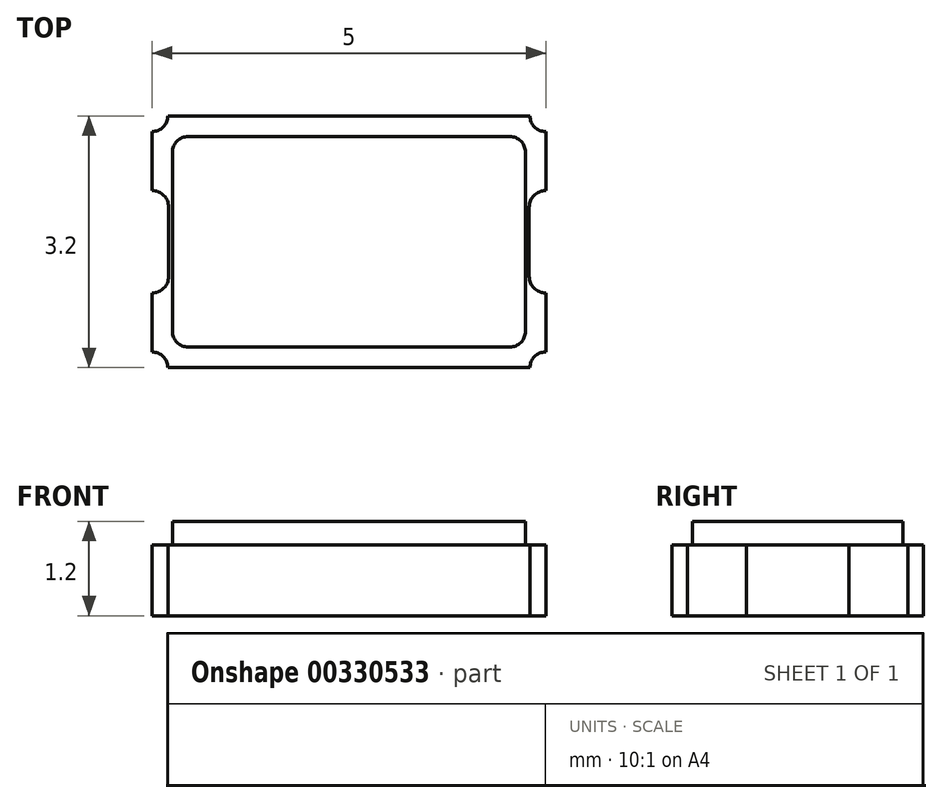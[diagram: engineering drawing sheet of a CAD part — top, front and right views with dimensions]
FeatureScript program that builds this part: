
annotation { "Feature Type Name" : "Feature", "Feature Type Description" : "" }
export const myFeature = defineFeature(function(context is Context, id is Id, definition is map)
    precondition{}
    {
        {
            var Q0;
            Q0=qCreatedBy(makeId("Top.planeOp"),FACE);
            var sketch = newSketch(context, id + "F0", { "sketchPlane" : qUnion([Q0])});
            skLineSegment(sketch, "E0.bottom", {"start": v(0, -1.6) * mm, "end": v(-2.3, -1.6) * mm});
            skLineSegment(sketch, "E0.top", {"start": v(0, 1.6) * mm, "end": v(-2.3, 1.6) * mm});
            skPoint(sketch, "E0.middle", {"position": v(0, 0) * mm});
            skArc(sketch, "E1", {"start": v(-2.3, 1.6) * mm, "mid": v(-2.36, 1.46) * mm, "end": v(-2.5, 1.4) * mm});
            skArc(sketch, "E2", {"start": v(-2.5, -1.4) * mm, "mid": v(-2.36, -1.46) * mm, "end": v(-2.3, -1.6) * mm});
            skLineSegment(sketch, "E3", {"start": v(0, 0) * mm, "end": v(-3.2, 0) * mm, "construction": true});
            skLineSegment(sketch, "E4", {"start": v(-2.5, 1.4) * mm, "end": v(-2.5, 0.65) * mm});
            skPoint(sketch, "E5.endSnap0", {"position": v(0, 1.6) * mm});
            skLineSegment(sketch, "E6", {"start": v(0, 1.6) * mm, "end": v(0, -2.23) * mm, "construction": true});
            skLineSegment(sketch, "E7.left", {"start": v(-2.3, -0.44) * mm, "end": v(-2.3, 0.44) * mm});
            skPoint(sketch, "E7.middle", {"position": v(-2.5, 0) * mm});
            skArc(sketch, "E8", {"start": v(-2.3, 0.44) * mm, "mid": v(-2.35, 0.59) * mm, "end": v(-2.5, 0.65) * mm});
            skArc(sketch, "E9", {"start": v(-2.3, -0.44) * mm, "mid": v(-2.35, -0.59) * mm, "end": v(-2.5, -0.65) * mm});
            skLineSegment(sketch, "E10.trimOffspring", {"start": v(-2.5, -0.65) * mm, "end": v(-2.5, -1.4) * mm});
            skPoint(sketch, "E11.orphan", {"position": v(-2.7, -0.44) * mm});
            skLineSegment(sketch, "E12.MirrorCS", {"start": v(2.5, -0.65) * mm, "end": v(2.5, -1.4) * mm});
            skLineSegment(sketch, "E13.MirrorCS", {"start": v(0, 0) * mm, "end": v(3.2, 0) * mm, "construction": true});
            skPoint(sketch, "E14.MirrorP", {"position": v(2.5, 0) * mm});
            skLineSegment(sketch, "E15.MirrorCS", {"start": v(2.5, 1.4) * mm, "end": v(2.5, 0.65) * mm});
            skLineSegment(sketch, "E16.MirrorCS", {"start": v(0, 1.6) * mm, "end": v(2.3, 1.6) * mm});
            skArc(sketch, "E17.MirrorCS", {"start": v(2.5, -1.4) * mm, "mid": v(2.36, -1.46) * mm, "end": v(2.3, -1.6) * mm});
            skLineSegment(sketch, "E18.MirrorCS", {"start": v(0, -1.6) * mm, "end": v(2.3, -1.6) * mm});
            skArc(sketch, "E19.MirrorCS", {"start": v(2.3, -0.44) * mm, "mid": v(2.35, -0.59) * mm, "end": v(2.5, -0.65) * mm});
            skLineSegment(sketch, "E20.MirrorCS", {"start": v(2.3, -0.44) * mm, "end": v(2.3, 0.44) * mm});
            skArc(sketch, "E21.MirrorCS", {"start": v(2.3, 0.44) * mm, "mid": v(2.35, 0.59) * mm, "end": v(2.5, 0.65) * mm});
            skPoint(sketch, "E22.MirrorP", {"position": v(2.7, -0.44) * mm});
            skArc(sketch, "E23.MirrorCS", {"start": v(2.3, 1.6) * mm, "mid": v(2.36, 1.46) * mm, "end": v(2.5, 1.4) * mm});
            skSolve(sketch);
        }
        {
            var Q0;
            Q0 = qSketchRegion(id + "F0", true);
            extrude(context, id + "F1", {"entities" : qUnion([Q0]), "depth" : .9 * mm, "offsetDistance" : 25 * mm});
        }
        {
            var Q0;
            Q0=makeQuery(id+"F1.opExtrude","CAP_FACE",FACE,{"disambiguationData":[OSD([sQuery(id+"F0.wireOp",EDGE,"E0.bottom"),sQuery(id+"F0.wireOp",EDGE,"E0.top"),sQuery(id+"F0.wireOp",EDGE,"E0.left"),sQuery(id+"F0.wireOp",EDGE,"E0.right"),sQuery(id+"F0.wireOp",EDGE,"E1"),sQuery(id+"F0.wireOp",EDGE,"E2"),sQuery(id+"F0.wireOp",EDGE,"xHCziCFv-irZE-u6qb-elKN-ItsrWE4nqJk2"),sQuery(id+"F0.wireOp",EDGE,"QKnBtfA7-HNCL-GVfP-wDzr-1vJRiM1siBZp")])],"isStart":false});
            var sketch = newSketch(context, id + "F2", { "sketchPlane" : qUnion([Q0])});
            skLineSegment(sketch, "E24.bottom", {"start": v(2.04, -1.34) * mm, "end": v(-2.04, -1.34) * mm});
            skLineSegment(sketch, "E24.top", {"start": v(2.04, 1.34) * mm, "end": v(-2.04, 1.34) * mm});
            skLineSegment(sketch, "E24.left", {"start": v(2.24, -1.14) * mm, "end": v(2.24, 1.14) * mm});
            skLineSegment(sketch, "E24.right", {"start": v(-2.24, -1.14) * mm, "end": v(-2.24, 1.14) * mm});
            skPoint(sketch, "E24.middle", {"position": v(0, 0) * mm});
            skPoint(sketch, "E25.visualSharp", {"position": v(-2.24, 1.34) * mm});
            skArc(sketch, "E25.filletArc", {"start": v(-2.04, 1.34) * mm, "mid": v(-2.18, 1.28) * mm, "end": v(-2.24, 1.14) * mm});
            skPoint(sketch, "E26.visualSharp", {"position": v(2.24, 1.34) * mm});
            skArc(sketch, "E26.filletArc", {"start": v(2.24, 1.14) * mm, "mid": v(2.18, 1.28) * mm, "end": v(2.04, 1.34) * mm});
            skPoint(sketch, "E27.visualSharp", {"position": v(2.24, -1.34) * mm});
            skArc(sketch, "E27.filletArc", {"start": v(2.04, -1.34) * mm, "mid": v(2.18, -1.28) * mm, "end": v(2.24, -1.14) * mm});
            skPoint(sketch, "E28.visualSharp", {"position": v(-2.24, -1.34) * mm});
            skArc(sketch, "E28.filletArc", {"start": v(-2.24, -1.14) * mm, "mid": v(-2.18, -1.28) * mm, "end": v(-2.04, -1.34) * mm});
            skSolve(sketch);
        }
        {
            var Q0;
            Q0 = qSketchRegion(id + "F2", true);
            extrude(context, id + "F3", {"entities" : qUnion([Q0]), "operationType" : NewBodyOperationType.ADD, "depth" : .3 * mm, "offsetDistance" : 25 * mm});
        }
    });
